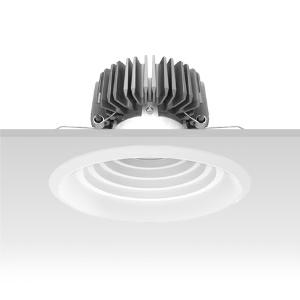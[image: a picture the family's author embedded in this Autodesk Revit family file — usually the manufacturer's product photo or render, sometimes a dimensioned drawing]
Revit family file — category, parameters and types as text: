
# Revit family: 3f_filippi_-_3f_reno_bianco_ampio_3f_filippi_-_30679_-_3f_reno_200_wh_3000-840_dali_wide
name_source: partatom
category: Lighting Fixtures
units: mm (PartAtom-declared; Revit-internal decimal feet)

## family parameters
Cut with Voids When Loaded = No
Host = Face
Light Source = No
Part Type = Normal
Room Calculation Point = No
Round Connector Dimension = Use Diameter
Shared = No

## types (1)
- 3F Filippi - 3F Reno Bianco Ampio (1 x LED, 2635 lm, 28 W, 4000 K)
    Apparent Load = 28 VA
    Approval mark = CE
    CIE Flux Codes = 80 97 100 100 100
    Color Rendering = 80
    Color Temperature = 4000 K
    Control Gear = Electronic transformer
    Default Elevation = 1800 mm
    Description = ILLUMINOTECHNICAL
Luminous efficiency 100% (DLOR 100%, ULOR 0%).
Initial luminous flux of the luminaire 2635 lm.
Direct symmetric wide distribution.
Installation Interdistance Transv.D = 1.56 x hu - Long.D = 1.56 x hu.
Tabular UGR (CIE 117 - 4H-8H; S=0.25H; 70/50/20): RUG 20.4 - 20.4.
Beam angle: 85° - 84°.
Luminous efficacy 94 lm/W.
Lifetime (L90/B10): 30000 h. (tq+25°C)
Lifetime (L85/B10): 50000 h. (tq+25°C)
Lifetime (L70/B10): 80000 h. (tq+25°C)
Sudden decreased luminous flux after 50000 hours: 0% (C0).
Photobiological safety in compliance with IEC/TR 62778: RG0 risk exempt, (IEC 62471).
In compliance with IEC/EN 62722-2-1 - IEC/EN 62717 standards.

SOURCE
Compact LED module 3000/840.
Energy efficiency class (UE 2019/2020 - UE 2019/2015): E.
CIE 13.3 Colour rendering index: CRI >80 (R9 <50%).
IES TM-30 Fidelity Index: Rf = 84 Rg = 95.
CCT nominal colour temperature 4000 K.
Colour initial tolerance (MacAdam): SDCM 3.
Zhaga Book 3 compliant.

MECHANICAL
Passive heat dissipator in die-casting aluminium, oversized, for optimum thermal management of the LED module.
Parabolic element with graduated/concentric rings in white polycarbonate.
Transparent external lens with glossy and satin differentiated surfaces, with a cooling and anti-insect system in methacrylate (PMMA).
Fastening spring clips in stainless steel.
Dimensions: diameter 216 mm, height 142 mm. Weight 1.495 kg.
IP44 protection degree for exposed part, IP20 for recessed part.
Mechanical strength to impacts IK04 (0.5 joule).
Glow-wire test resistance 650°C.

ELECTRICAL
Wiring on a separate unit.
Halogen Free DALI-2 DATI (Parts 251, 252, 253), PUSH-DIM, electronic wiring 230V-50/60Hz, power factor 0.97 at full load, THD <25%, constant output current, SELV, class II, 1 driver, 1 DALI addresse.
Power of the luminaire 28 W.
ENEC - CE.
SAFE FLICKER: PstLM=<1 and SVM=<0.4 (IEC TR 61547-1 and IEC TR 63158), to ensure a more comfortable and safe light.
Luminaire compliant with EN 60598-2-22 for power supply from a centralised emergency system CPSS (Central Power Supply System), not incorporated in the luminaire - high risk areas excluded. The default power and flux are 100% in AC and 100% in DC.
Ambient temperature from 0°C to +25°C.
Temperature class T6 max 85°C.
Relative humidity UR: <85%.

INSTALLATION
Pull-up recessed fitting.
False ceiling carving: 200 mm.
All accessories dedicated to this product are available on the Catalog and on our website www.3F-Filippi.com.

APPLICATIONS
Environments: architectural, commercial, exhibition areas, transit areas, corridors, shops, display windows, service areas.
In false ceilings with narrow voids.

LIGHT MANAGEMENT
Recommended minimum setting: 10%.
The luminaire, equipped with (DALI-2 DATI) driver, can be controlled manually with 3F Easy Dim technology or automatically/manually with wired or wireless DALI/D2D control systems.
The D2D driver guarantees interoperability with other devices with the same certification by making the following information available:
Device Data (Part 251), Energy Report (Part 252), Diagnosis & Maintenance (Part 253).
In electrical systems without a regulation system (manual or automatic) and DALI bus, a suitable jumper must be made on the DA-DA terminals of the appliance.

WARNING
Luminaire designed for disposal/recycling at end-of-life.
Replaceable (LED only) light source by a professional. Replaceable control gear by a professional.
    Height = 0 mm  [stored 0 ft]
    Lamp = 1 x LED
    Lamp Light Flux = 2635 lm
    Lamp Power = 28 W
    Lamp count = 1
    Length = 216 mm
    Lifetime = 50000 h
    Luminous efficacy = 94 lm/W
    Manufacturer = 3F Filippi
    ModVariant = No
    Model = 3F Filippi - 30679 - 3F Reno 200 WH 3000-840 DALI WIDE
    Mounting Place = Ceiling
    Mounting Type = Recessed
    Number of Poles = 1
    OnlyDefault = Yes
    Power Factor = 1
    Product Name = 3F Filippi - 3F Reno Bianco Ampio
    Product group = recessed luminaire
    ProductGroupID = 4
    Protection Class = Protection class II
    Protection Degree = IP 20
    RLX_Detail_Level = 1
    RLX_Emergency_Light_Flux = 0 lm
    RLX_Emergency_Type = 0
    RLX_Emergency_Type_DB = No
    RlxData = <blob elided: 95001 chars, md5=7e4465ba>
    Socket = socket
    Standby Power = 0 W
    System Light Flux = 2635 lm
    System Power = 28 W
    Type Comments = Product without accessories
    Type Image = 3ffilippi_3f_reno_200_wh_2500_3000_4000.jpg
    URL = http://relux.com
    VarID = ---
    Voltage = 0 V
    Weight = 0.00 kg
    Width = 0 mm  [stored 0 ft]

note: [stored X ft] marks values corroborated as IEEE doubles in the binary element streams (Revit-internal decimal feet)

## geometry (parser evidence)
native form markers: Blend x4, Sweep x10
no freeform markers — native parametric forms only
